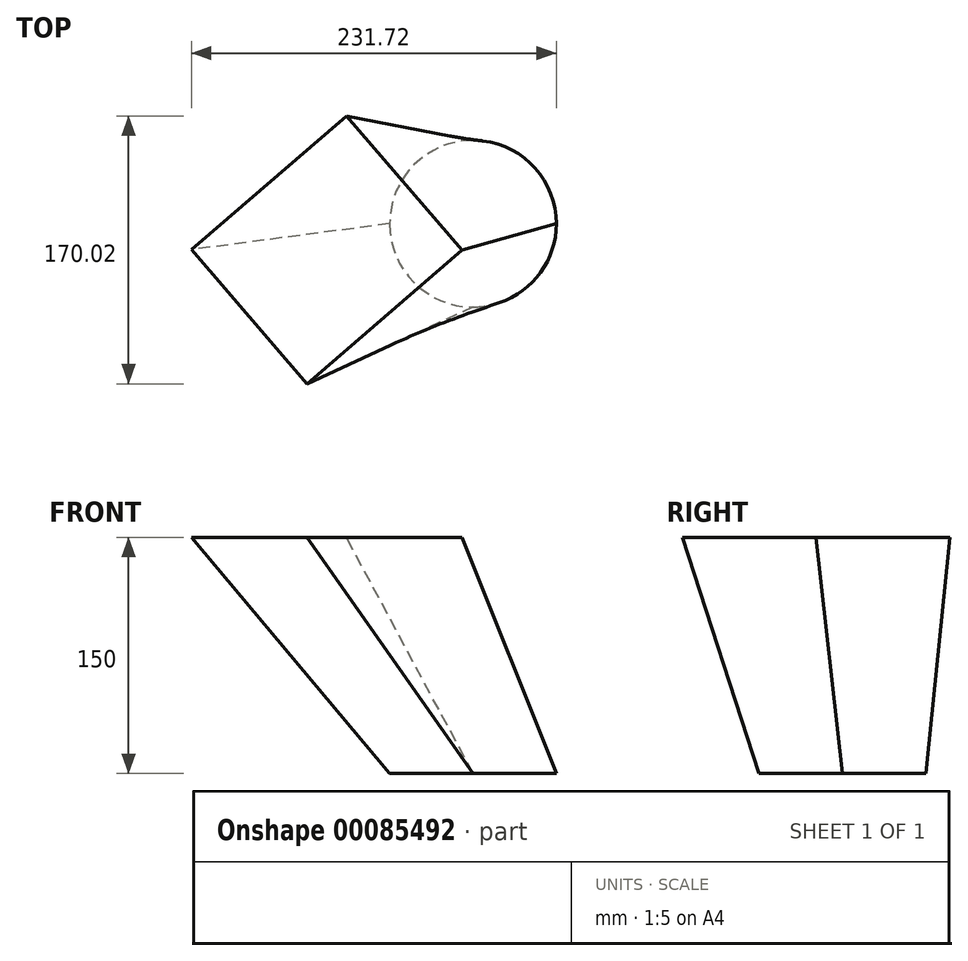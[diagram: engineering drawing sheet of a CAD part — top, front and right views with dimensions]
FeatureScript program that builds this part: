
annotation { "Feature Type Name" : "Feature", "Feature Type Description" : "" }
export const myFeature = defineFeature(function(context is Context, id is Id, definition is map)
    precondition{}
    {
        {
            var Q0;
            Q0=qCreatedBy(makeId("Top.planeOp"),FACE);
            var sketch = newSketch(context, id + "F0", { "sketchPlane" : qUnion([Q0])});
            skCircle(sketch, "E0", {"center": v(0, 0) * mm, "radius": 52.91 * mm});
            skPoint(sketch, "E1", {"position": v(52.91, 0) * mm});
            skPoint(sketch, "E2", {"position": v(0, 52.91) * mm});
            skPoint(sketch, "E3", {"position": v(0, -52.91) * mm});
            skPoint(sketch, "E4", {"position": v(-52.91, 0) * mm});
            skSolve(sketch);
        }
        {
            var Q0;
            Q0=qCreatedBy(makeId("Top.planeOp"),FACE);
            cPlane(context, id + "F1", {"entities" : qUnion([Q0]), "cplaneType" : CPlaneType.OFFSET, "offset" : 150 * mm, "width" : 150 * mm, "height" : 150 * mm});
        }
        {
            var Q0;
            Q0=qCreatedBy(id+"F1.planeOp",FACE);
            var sketch = newSketch(context, id + "F2", { "sketchPlane" : qUnion([Q0])});
            skLineSegment(sketch, "E5.bottom", {"start": v(-6.99, -16.85) * mm, "end": v(-105.34, -101.67) * mm});
            skLineSegment(sketch, "E5.top", {"start": v(-80.46, 68.35) * mm, "end": v(-178.81, -16.47) * mm});
            skLineSegment(sketch, "E5.left", {"start": v(-6.99, -16.85) * mm, "end": v(-80.46, 68.35) * mm});
            skLineSegment(sketch, "E5.right", {"start": v(-105.34, -101.67) * mm, "end": v(-178.81, -16.47) * mm});
            skPoint(sketch, "E5.middle", {"position": v(-92.9, -16.66) * mm});
            skSolve(sketch);
        }
        {
            var Q0;
            Q0=makeQuery(id+"F0.imprint","IMPRINT",FACE,{"disambiguationData":[TD([[makeQuery(id+"F0.imprint","IMPRINT",EDGE,{"derivedFrom":sQuery(id+"F0.wireOp",EDGE,"E0")}),1.0]])]});
            var Q1;
            Q1=makeQuery(id+"F2.imprint","IMPRINT",FACE,{"disambiguationData":[TD([[makeQuery(id+"F2.imprint","IMPRINT",EDGE,{"derivedFrom":sQuery(id+"F2.wireOp",EDGE,"E5.bottom")}),-1.0]])]});
            var Q2;
            Q2=sQuery(id+"F0.wireOp",VERTEX,"E3");
            var Q3;
            Q3=sQuery(id+"F2.wireOp",VERTEX,"E5.right.start");
            loft(context, id + "F3", {"sheetProfilesArray" : [{ "sheetProfileEntities" : qUnion([Q0]) }, { "sheetProfileEntities" : qUnion([Q1]) }], "matchConnections" : true, "connections" : [{ "connectionEntities" : qUnion([Q2, Q3]), "connectionEdgeQueries" : qUnion([]), "connectionEdgeParameters" : [] }]});
        }
    });
